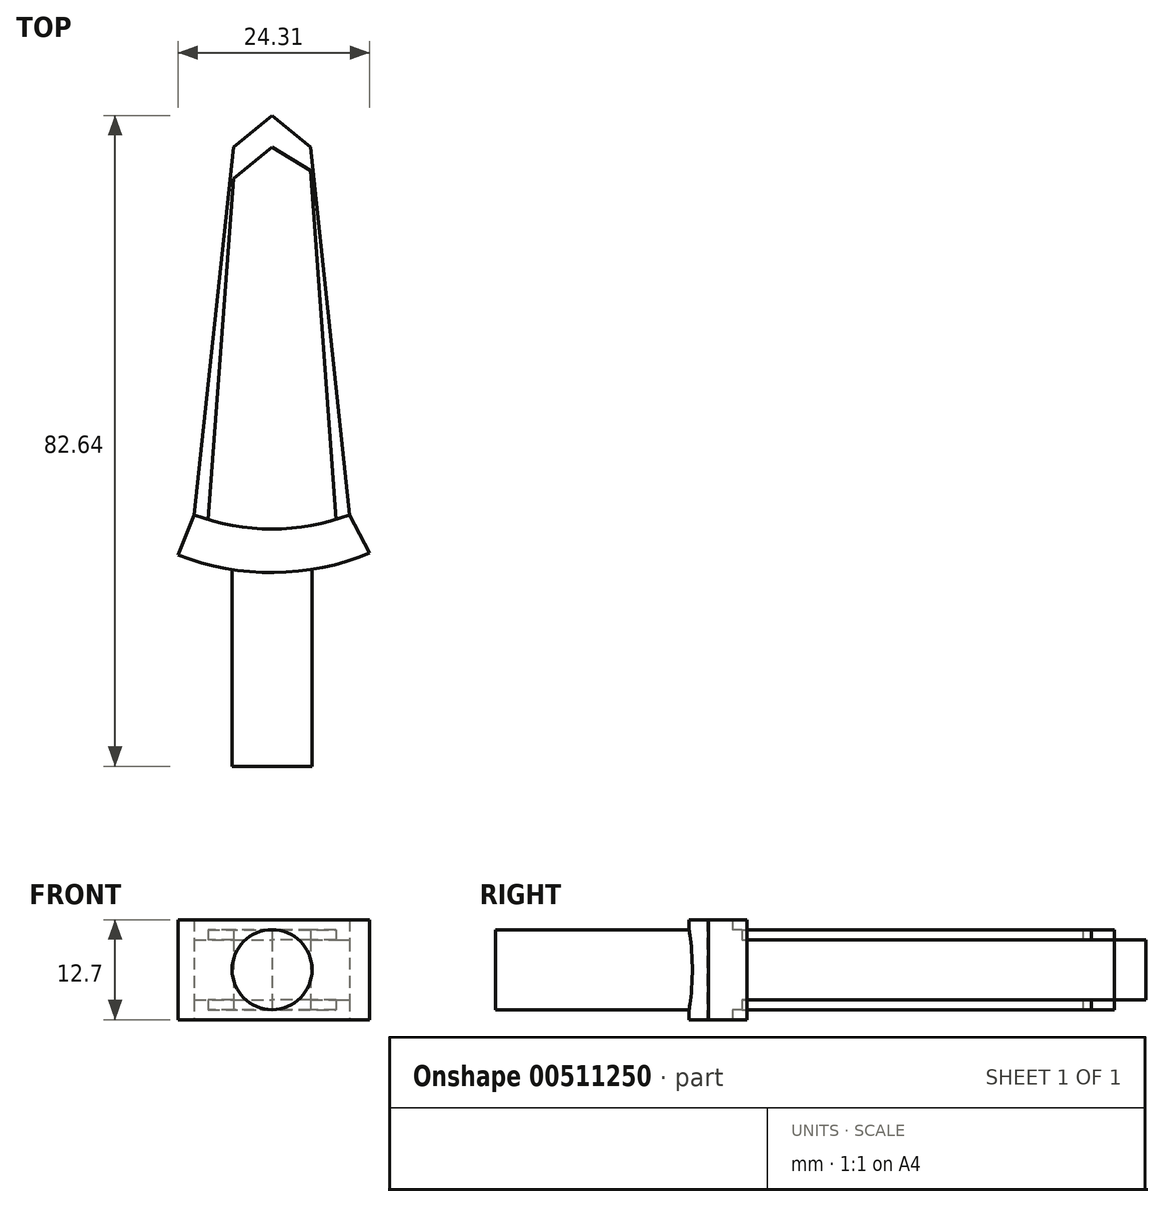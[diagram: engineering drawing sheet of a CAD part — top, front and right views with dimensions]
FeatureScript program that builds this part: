
annotation { "Feature Type Name" : "Feature", "Feature Type Description" : "" }
export const myFeature = defineFeature(function(context is Context, id is Id, definition is map)
    precondition{}
    {
        {
            var Q0;
            Q0=qCreatedBy(makeId("Top.planeOp"),FACE);
            var sketch = newSketch(context, id + "F0", { "sketchPlane" : qUnion([Q0])});
            skArc(sketch, "E0", {"start": v(-9.9, 6.52) * mm, "mid": v(-0.02, 4.72) * mm, "end": v(9.85, 6.52) * mm});
            skLineSegment(sketch, "E1", {"start": v(-9.9, 6.52) * mm, "end": v(-11.93, 1.43) * mm});
            skLineSegment(sketch, "E2", {"start": v(9.85, 6.52) * mm, "end": v(12.38, 1.66) * mm});
            skArc(sketch, "E3", {"start": v(-11.93, 1.43) * mm, "mid": v(0.25, -0.8) * mm, "end": v(12.38, 1.66) * mm});
            skLineSegment(sketch, "E4", {"start": v(-9.9, 6.52) * mm, "end": v(-4.9, 53.24) * mm});
            skLineSegment(sketch, "E5", {"start": v(4.9, 53.24) * mm, "end": v(9.85, 6.52) * mm});
            skLineSegment(sketch, "E6", {"start": v(-4.9, 53.24) * mm, "end": v(0, 57.24) * mm});
            skLineSegment(sketch, "E7", {"start": v(4.9, 53.24) * mm, "end": v(0, 57.24) * mm});
            skLineSegment(sketch, "E8", {"start": v(0, 53.24) * mm, "end": v(-4.9, 49.24) * mm});
            skLineSegment(sketch, "E9", {"start": v(-4.9, 49.24) * mm, "end": v(-8.15, 5.93) * mm});
            skLineSegment(sketch, "E10", {"start": v(4.9, 50.28) * mm, "end": v(0, 53.24) * mm});
            skLineSegment(sketch, "E11", {"start": v(8.11, 5.93) * mm, "end": v(4.9, 50.28) * mm});
            skSolve(sketch);
        }
        {
            var Q0;
            Q0=makeQuery(id+"F0.imprint","IMPRINT",FACE,{"disambiguationData":[TD([[makeQuery(id+"F0.imprint","IMPRINT",EDGE,{"derivedFrom":sQuery(id+"F0.wireOp",EDGE,"E0")}),-1.0]])]});
            extrude(context, id + "F1", {"entities" : qUnion([Q0]), "endBound" : BoundingType.SYMMETRIC, "depth" : 12.7 * mm});
        }
        {
            var Q0;
            Q0=qCreatedBy(makeId("Front.planeOp"),FACE);
            var sketch = newSketch(context, id + "F2", { "sketchPlane" : qUnion([Q0])});
            skCircle(sketch, "E12", {"center": v(0, 0) * mm, "radius": 5.08 * mm});
            skSolve(sketch);
        }
        {
            var Q0;
            Q0 = qSketchRegion(id + "F2", true);
            extrude(context, id + "F3", {"entities" : qUnion([Q0]), "operationType" : NewBodyOperationType.ADD, "depth" : 25.4 * mm});
        }
        {
            var Q0;
            {var subQ0=sQuery(id+"F0.wireOp",EDGE,"E4");Q0=makeQuery(id+"F0.imprint","IMPRINT",FACE,{"disambiguationData":[TD([[makeQuery(id+"F0.imprint","IMPRINT",EDGE,{"derivedFrom":subQ0}),-1.0]])]});}
            extrude(context, id + "F4", {"entities" : qUnion([Q0]), "operationType" : NewBodyOperationType.ADD, "endBound" : BoundingType.SYMMETRIC, "depth" : 7.62 * mm});
        }
        {
            var Q0;
            Q0=makeQuery(id+"F0.imprint","IMPRINT",FACE,{"disambiguationData":[TD([[makeQuery(id+"F0.imprint","IMPRINT",EDGE,{"derivedFrom":sQuery(id+"F0.wireOp",EDGE,"E8")}),1.0]])]});
            extrude(context, id + "F5", {"entities" : qUnion([Q0]), "operationType" : NewBodyOperationType.ADD, "endBound" : BoundingType.SYMMETRIC, "depth" : 10.16 * mm});
        }
    });
